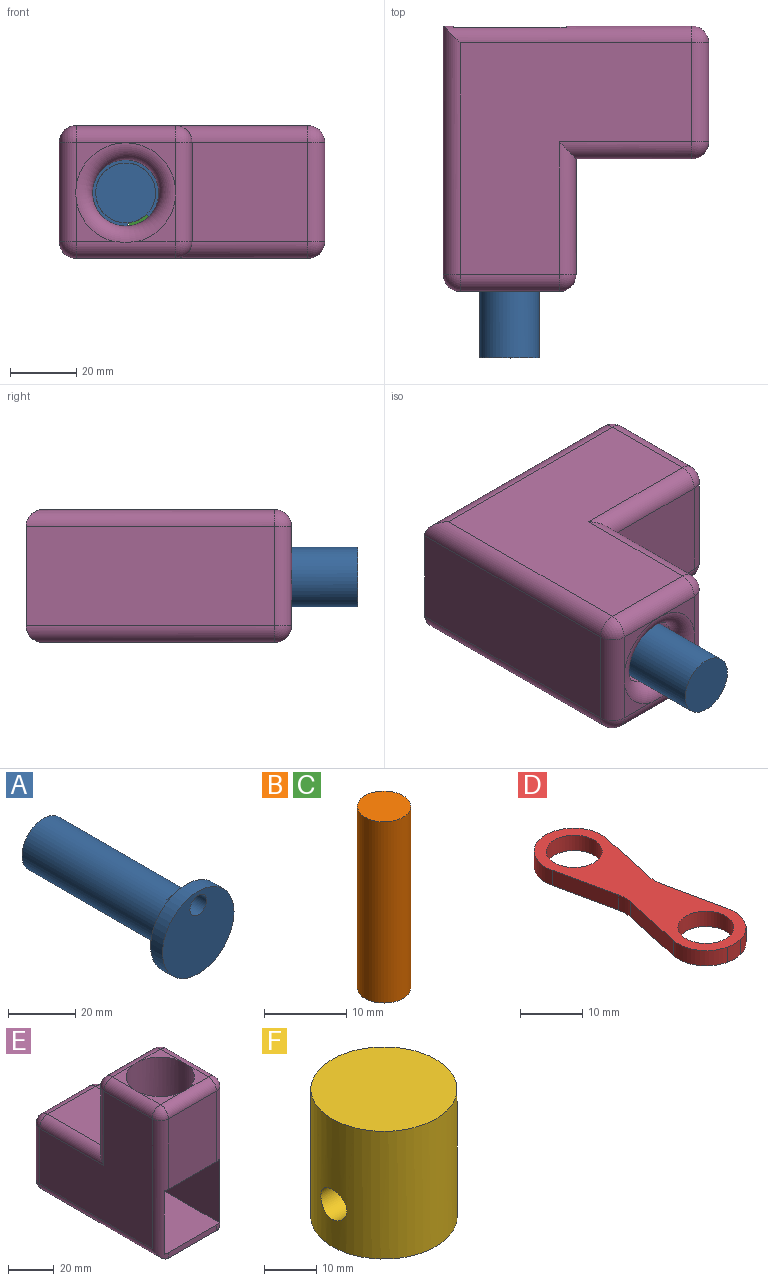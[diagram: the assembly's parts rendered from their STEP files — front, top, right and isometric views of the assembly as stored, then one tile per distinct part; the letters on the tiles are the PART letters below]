
ASSEMBLY  parts=6 mates=7
PART A: 7 faces, bbox 30x65x30 mm
  f0: cylinder r=9mm len=60mm, axis (0,1,0), area 3360.9mm2, adj f1,f4,f5,f6
  f1: plane 18x18mm, normal (0,1,0), area 254.5mm2, adj f0
  f2: cylinder r=15mm len=30mm, axis (0,1,0), area 471.2mm2, adj f3,f4
  f3: plane 30x30mm, normal (0,-1,0), area 668.4mm2, adj f2,f6
  f4: plane 30x30mm, normal (0,1,0), area 424.9mm2, adj f0,f2,f6
  f5: plane 6.26x2.5mm, normal (0,-1,0), area 11mm2, adj f0,f6
  f6: cylinder r=3.5mm len=10mm, axis (0,-1,0), area 148.7mm2, adj f0,f3,f4,f5
PART B: 3 faces, bbox 6.5x6.5x27 mm
  f0: cylinder r=3.25mm len=27mm, axis (0,0,-1), area 551.3mm2, adj f1,f2
  f1: plane 6.5x6.5mm, normal (0,0,1), area 33.2mm2, adj f0
  f2: plane 6.5x6.5mm, normal (0,0,-1), area 33.2mm2, adj f0
PART C: same geometry as B
PART D: 16 faces, bbox 12.8x43x3 mm
  f0: cylinder r=6.35mm len=7.53mm, axis (0,0,-1), area 29.6mm2, adj f1,f13,f14,f15
  f1: cylinder r=6.5mm len=3mm, axis (0,0,-1), area 9mm2, adj f0,f2,f14,f15
  f2: cylinder r=6.35mm len=7.53mm, axis (0,0,-1), area 29.6mm2, adj f1,f3,f14,f15
  f3: plane 12.46x3mm, normal (0.98,0.21,0), area 38.2mm2, adj f2,f4,f14,f15
  f4: cylinder r=6.35mm len=3mm, axis (0,0,-1), area 8.1mm2, adj f3,f5,f14,f15
  f5: plane 12.46x3mm, normal (0.98,-0.21,0), area 38.2mm2, adj f4,f6,f14,f15
  f6: cylinder r=6.35mm len=7.53mm, axis (0,0,-1), area 29.6mm2, adj f5,f7,f14,f15
  f7: cylinder r=6.5mm len=3mm, axis (0,0,-1), area 9mm2, adj f6,f8,f14,f15
  f8: cylinder r=6.35mm len=7.53mm, axis (0,0,-1), area 29.6mm2, adj f7,f9,f14,f15
  f9: plane 12.46x3mm, normal (-0.98,-0.21,0), area 38.2mm2, adj f8,f10,f14,f15
  f10: cylinder r=6.35mm len=3mm, axis (0,0,-1), area 8.1mm2, adj f9,f13,f14,f15
  f11: cylinder r=4.5mm len=9mm, axis (0,0,-1), area 84.8mm2, adj f14,f15
  f12: cylinder r=4.5mm len=9mm, axis (0,0,-1), area 84.8mm2, adj f14,f15
  f13: plane 12.46x3mm, normal (-0.98,0.21,0), area 38.2mm2, adj f0,f10,f14,f15
  f14: plane 43x12.77mm, normal (0,0,1), area 296.6mm2, adj f0,f1,f2,f3,f4,f5,f6,f7
  f15: plane 43x12.77mm, normal (0,0,-1), area 296.6mm2, adj f0,f1,f2,f3,f4,f5,f6,f7
PART E: 46 faces, bbox 40.5x80x80.2 mm
  f0: plane 29.84x3mm, normal (0,-1,0), area 89.5mm2, adj f11,f16,f31,f32
  f1: plane 13.37x13.37mm, normal (0,0,1), area 46.1mm2, adj f19,f22,f23
  f2: plane 13.37x13.37mm, normal (0,0,1), area 46.1mm2, adj f19,f21,f22
  f3: plane 13.37x13.37mm, normal (0,0,1), area 46.1mm2, adj f19,f23,f24
  f4: plane 12.46x11.34mm, normal (0,1,0), area 41.2mm2, adj f43,f44,f45
  f5: plane 12.46x11.34mm, normal (0,1,0), area 41.2mm2, adj f42,f43,f45
  f6: plane 37.92x29.84mm, normal (0,-1,0), area 1131.5mm2, adj f14,f23,f31,f32
  f7: plane 34.92x29.84mm, normal (0,0,1), area 1042mm2, adj f12,f33,f34,f42
  f8: plane 69.84x69.84mm, normal (-1,0,0), area 3277.6mm2, adj f22,f30,f31,f34,f35,f43
  f9: plane 69.84x69.84mm, normal (1,0,0), area 3277.6mm2, adj f24,f29,f32,f33,f36,f37
  f10: plane 29.84x13mm, normal (0,1,0), area 96.6mm2, adj f37,f42,f44,f45
  f11: plane 74.92x29.84mm, normal (0,0,-1), area 2235.6mm2, adj f0,f35,f36,f44
  f12: plane 34.92x29.84mm, normal (0,1,0), area 1042mm2, adj f7,f21,f29,f30
  f13: plane 13.37x13.37mm, normal (0,0,1), area 46.1mm2, adj f19,f21,f24
  f14: plane 40x34mm, normal (0,0,-1), area 652.5mm2, adj f6,f15,f17,f18,f19,f31,f32
  f15: plane 39.55x34mm, normal (1,0,0), area 1344.9mm2, adj f14,f16,f18,f31
  f16: plane 40x34mm, normal (0,0,1), area 1359.4mm2, adj f0,f15,f17,f18,f31,f32
  f17: plane 39.55x34mm, normal (-1,0,0), area 1344.9mm2, adj f14,f16,f18,f32
  f18: plane 34x34mm, normal (0,-1,0), area 841.8mm2, adj f14,f15,f16,f17,f20
  f19: cylinder r=15mm len=43mm, axis (0,0,1), area 4052.7mm2, adj f1,f2,f3,f13,f14,f21,f22,f23
  f20: cylinder r=10mm len=34.92mm, axis (0,1,0), area 2194.1mm2, adj f18,f45
  f21: cylinder r=5.08mm len=29.84mm, axis (1,0,0), area 238.1mm2, adj f2,f12,f13,f19,f25,f26
  f22: cylinder r=5.08mm len=29.84mm, axis (0,1,0), area 238.1mm2, adj f1,f2,f8,f19,f26,f27
  f23: cylinder r=5.08mm len=29.84mm, axis (-1,0,0), area 238.1mm2, adj f1,f3,f6,f19,f27,f28
  f24: cylinder r=5.08mm len=29.84mm, axis (0,-1,0), area 238.1mm2, adj f3,f9,f13,f19,f25,f28
  f25: sphere r=5.08mm, area 40.5mm2, adj f21,f24,f29
  f26: sphere r=5.08mm, area 40.5mm2, adj f21,f22,f30
  f27: sphere r=5.08mm, area 40.5mm2, adj f22,f23,f31
  f28: sphere r=5.08mm, area 40.5mm2, adj f23,f24,f32
  f29: cylinder r=5.08mm len=40mm, axis (0,0,-1), area 293.4mm2, adj f9,f12,f25,f33
  f30: cylinder r=5.08mm len=40mm, axis (0,0,1), area 293.4mm2, adj f8,f12,f26,f34
  f31: cylinder r=5.08mm len=74.92mm, axis (0,0,-1), area 510.2mm2, adj f0,f6,f8,f14,f15,f16,f27,f35
  f32: cylinder r=5.08mm len=74.92mm, axis (0,0,1), area 510.2mm2, adj f0,f6,f9,f14,f16,f17,f28,f36
  f33: cylinder r=5.08mm len=40mm, axis (0,-1,0), area 293.4mm2, adj f7,f9,f29,f38
  f34: cylinder r=5.08mm len=40mm, axis (0,1,0), area 293.4mm2, adj f7,f8,f30,f39
  f35: cylinder r=5.08mm len=74.92mm, axis (0,-1,0), area 583.1mm2, adj f8,f11,f31,f40
  f36: cylinder r=5.08mm len=74.92mm, axis (0,1,0), area 583.1mm2, adj f9,f11,f32,f41
  f37: cylinder r=5.08mm len=29.84mm, axis (0,0,-1), area 238.1mm2, adj f9,f10,f38,f41
  f38: sphere r=5.08mm, area 40.5mm2, adj f33,f37,f42
  f39: sphere r=5.08mm, area 40.5mm2, adj f34,f42,f43
  f40: sphere r=5.08mm, area 40.5mm2, adj f35,f43,f44
  f41: sphere r=5.08mm, area 40.5mm2, adj f36,f37,f44
  f42: cylinder r=5.08mm len=29.84mm, axis (1,0,0), area 237.9mm2, adj f5,f7,f10,f38,f39,f45
  f43: cylinder r=5.08mm len=29.84mm, axis (0,0,1), area 237.1mm2, adj f4,f5,f8,f39,f40,f45
  f44: cylinder r=5.08mm len=29.84mm, axis (-1,0,0), area 237.9mm2, adj f4,f10,f11,f40,f41,f45
  f45: torus R=15.08mm, axis (0,1,0), area 592.5mm2, adj f4,f5,f10,f20,f42,f43,f44
PART F: 7 faces, bbox 28x28x29.9 mm
  f0: cylinder r=14mm len=29.92mm, axis (0,0,-1), area 2554.3mm2, adj f1,f4,f5,f6
  f1: plane 28x28mm, normal (0,0,1), area 615.8mm2, adj f0
  f2: cylinder r=9mm len=19.92mm, axis (0,0,-1), area 1047.9mm2, adj f3,f4,f5,f6
  f3: plane 18x18mm, normal (0,0,-1), area 254.5mm2, adj f2
  f4: cylinder r=3.5mm len=7mm, axis (1,0,0), area 112.8mm2, adj f0,f2
  f5: cylinder r=3.5mm len=7mm, axis (1,0,0), area 112.8mm2, adj f0,f2
  f6: cone r=14.08mm half-angle=45deg, axis (0,0,-1), area 510.9mm2, adj f0,f2
PLACE A rot(axis=(-0.98,0,-0.21),180deg) t=(-12.72,-67.28,-20.27)mm
PLACE B rot(axis=(0,-0.71,0.71),180deg) t=(19.94,26.76,-20)mm
PLACE C rot(axis=(0.15,0.7,-0.7),162.7deg) t=(-8.56,19.72,-29.37)mm
PLACE D rot(axis=(0.46,-0.63,0.63),131deg) t=(19.94,12.83,-20)mm
PLACE E rot(axis=(0.71,0,0.71),180deg) t=(-32.72,-1.14,-20.27)mm
PLACE F rot(axis=(0.58,0.58,0.58),120deg) t=(9.94,12.72,-20)mm
MATE fastened C.f0 <-> A.f6  axis (0,1,0) through (-8.56,-7.28,-29.37)mm
MATE planar A.f4 <-> E.f18  axis (0,-1,0) through (-13.01,-7.28,-19.63)mm
MATE cylindrical D.f1 <-> B.f0  axis (0,1,0) through (19.94,12.83,-20)mm
MATE cylindrical D.f7 <-> C.f0  axis (0,1,0) through (-8.56,12.83,-29.37)mm
MATE cylindrical A.f0 <-> E.f20  axis (0,-1,0) through (-12.72,-67.28,-20.27)mm
MATE slider F.f0 <-> E.f19  axis (1,0,0) through (39.94,12.72,-20)mm
MATE fastened B.f0 <-> F.f4  axis (0,1,0) through (19.94,26.76,-20)mm
